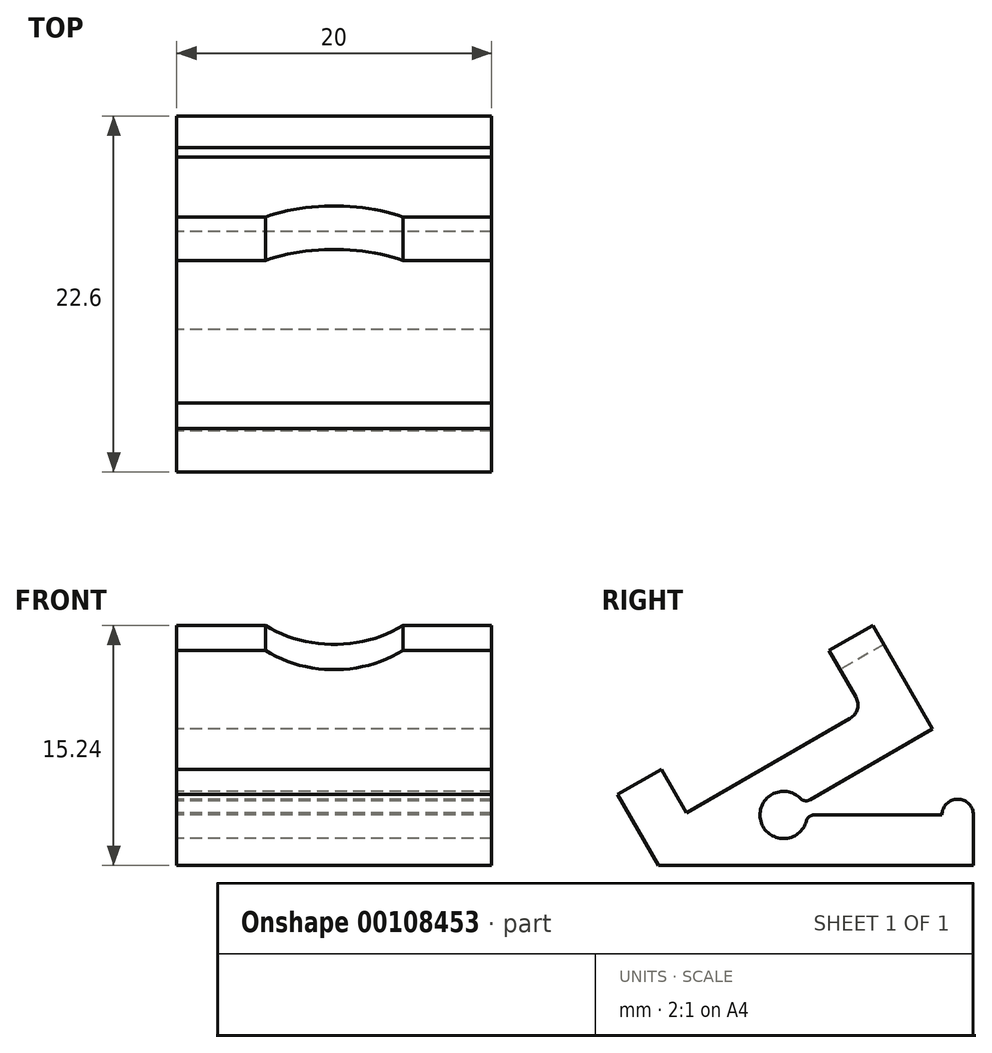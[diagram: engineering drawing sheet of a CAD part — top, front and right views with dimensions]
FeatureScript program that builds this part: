
annotation { "Feature Type Name" : "Feature", "Feature Type Description" : "" }
export const myFeature = defineFeature(function(context is Context, id is Id, definition is map)
    precondition{}
    {
        {
            var Q0;
            Q0=qCreatedBy(makeId("Right.planeOp"),FACE);
            var sketch = newSketch(context, id + "F0", { "sketchPlane" : qUnion([Q0])});
            skLineSegment(sketch, "E0", {"start": v(0, 0) * mm, "end": v(-2.6, 4.5) * mm});
            skLineSegment(sketch, "E1", {"start": v(-2.6, 4.5) * mm, "end": v(0.17, 6.1) * mm});
            skLineSegment(sketch, "E2", {"start": v(0.17, 6.1) * mm, "end": v(1.77, 3.33) * mm});
            skLineSegment(sketch, "E3", {"start": v(12.53, 10.7) * mm, "end": v(10.83, 13.64) * mm});
            skLineSegment(sketch, "E4", {"start": v(10.83, 13.64) * mm, "end": v(13.6, 15.24) * mm});
            skLineSegment(sketch, "E5", {"start": v(13.6, 15.24) * mm, "end": v(17.4, 8.66) * mm});
            skLineSegment(sketch, "E6", {"start": v(17.4, 8.66) * mm, "end": v(9.62, 4.17) * mm});
            skLineSegment(sketch, "E7", {"start": v(9.88, 3.2) * mm, "end": v(18, 3.2) * mm});
            skLineSegment(sketch, "E8", {"start": v(20, 3.2) * mm, "end": v(20, 0) * mm});
            skLineSegment(sketch, "E9", {"start": v(20, 0) * mm, "end": v(0, 0) * mm});
            skPoint(sketch, "E10.visualSharp", {"position": v(7.94, 3.2) * mm});
            skPoint(sketch, "E11.visualSharp", {"position": v(17.4, 8.66) * mm});
            skArc(sketch, "E12", {"start": v(20, 3.2) * mm, "mid": v(19, 4.2) * mm, "end": v(18, 3.2) * mm});
            skLineSegment(sketch, "E13", {"start": v(1.77, 3.33) * mm, "end": v(12.16, 9.33) * mm});
            skPoint(sketch, "E14.visualSharp", {"position": v(13.03, 9.83) * mm});
            skArc(sketch, "E14.filletArc", {"start": v(12.16, 9.33) * mm, "mid": v(12.63, 9.94) * mm, "end": v(12.53, 10.7) * mm});
            skArc(sketch, "E15", {"start": v(9.01, 4.25) * mm, "mid": v(6.5, 2.81) * mm, "end": v(9.4, 2.82) * mm});
            skPoint(sketch, "E16.visualSharp", {"position": v(9.24, 3.95) * mm});
            skArc(sketch, "E16.filletArc", {"start": v(9.01, 4.25) * mm, "mid": v(9.3, 4.1) * mm, "end": v(9.62, 4.17) * mm});
            skPoint(sketch, "E17.visualSharp", {"position": v(9.44, 3.2) * mm});
            skArc(sketch, "E17.filletArc", {"start": v(9.88, 3.2) * mm, "mid": v(9.57, 3.1) * mm, "end": v(9.4, 2.83) * mm});
            skSolve(sketch);
        }
        {
            var Q0;
            Q0=qSketchRegion(id+"F0",true);
            extrude(context, id + "F1", {"entities" : qUnion([Q0]), "endBound" : BoundingType.SYMMETRIC, "depth" : 20 * mm});
        }
        {
            var Q0;
            Q0=makeQuery(id+"F1.opExtrude","SWEPT_FACE",FACE,{"disambiguationData":[OSD([sQuery(id+"F0.wireOp",EDGE,"E3")])]});
            var sketch = newSketch(context, id + "F2", { "sketchPlane" : qUnion([Q0])});
            skArc(sketch, "E18", {"start": v(-4.36, 6.4) * mm, "mid": v(0, 5) * mm, "end": v(4.36, 6.4) * mm});
            skLineSegment(sketch, "E19", {"start": v(-4.36, 6.4) * mm, "end": v(4.36, 6.4) * mm});
            skSolve(sketch);
        }
        {
            var Q0;
            Q0=qSketchRegion(id+"F2",true);
            var Q1;
            Q1=makeQuery(id+"F1.opExtrude","SWEPT_FACE",FACE,{"disambiguationData":[OSD([sQuery(id+"F0.wireOp",EDGE,"E5")])]});
            extrude(context, id + "F3", {"entities" : qUnion([Q0]), "operationType" : NewBodyOperationType.REMOVE, "endBound" : BoundingType.UP_TO_SURFACE, "oppositeDirection" : true, "endBoundEntityFace" : qUnion([Q1]), "depth" : 25 * mm});
        }
    });
